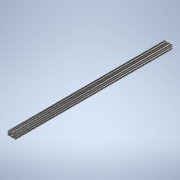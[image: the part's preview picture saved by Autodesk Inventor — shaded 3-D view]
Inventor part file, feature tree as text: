
AUTODESK INVENTOR PART (.ipt)
format: ipt  version: 2020 (Build 240168000, 168)  size: 363,520 bytes
history: native  units: in
note: dims shown in document units (in); Inventor stores cm internally (conversion verified against a paired STEP export)
features: sketch x2, extrude x1
ambient origin geometry x8: Origin, YZ Plane, XZ Plane, XY Plane, X Axis, Y Axis, Z Axis, Center Point
bodies: Solid1 (feature_tree)
feature tree (3):
  extrude  "Extrusion1"  [1 undecoded]
  sketch  "Sketch2"
  sketch  "Sketch1"  dims[d0=39.0in d1=0.0in]
note: 1 required parameter value undecoded (feature->parameter linkage not recoverable at this tier; creation-order binding heuristic only, values carry confidence <= 0.55)
